# Revit family: Sunshade-Corner-Kawneer-Curtain_Wall-Inside_90
name_source: partatom
category: Specialty Equipment
revit_build: Autodesk Revit 2015 (Build: 20140905_0730(x64)
units: mm (PartAtom-declared; Revit-internal decimal feet)

## types (1)
- 30"-Circular-Square
    Angle 1 = 135.00°
    Blade 1 Location = 0' - 0"
    Blade 2 Location = 0' - 0"
    Blade 3 Location = 0' - 0"
    Blade 4 Location = 0' - 0"
    Blade 5 Location = 0' - 0"
    Blade 6 Location = 0' - 0"
    Blade Distance = 0' - 5"
    Blade Type = Blade-Kawneer-Angle_Cut-Circular : Versoleil
    Bottom Fascia Offset = 2' - 5 1/4"
    CTRL Angle = 135.00°
    CTRL Fascia Location = 0' - 0"
    CTRL Length of Blade = 3' - 5 9/16"
    CTRL Outrigger Angle = 0.00°
    Default Elevation = 4' - 0"
    Description = Rounded Outrigger, Bullnose Fascias
    Distance Blade 1 and 2 = 0' - 0"
    Distance Blade 2 and 3 = 0' - 0"
    Distance Blade 3 and 4 = 0' - 0"
    Distance Blade 4 and 5 = 0' - 0"
    Distance Blade 5 and 6 = 0' - 0"
    Fascia Type = Fascia-Kawneer-Inside_Angle_Cut-Rectangular : Versoleil
    Finish = Aluminum - Kawneer - Clear
    Has 5th Blade = Yes
    Has 6th Blade = No
    Height of Blade 1 = 0' - 5"
    Height of Bottom Fascia = 2' - 6"
    Length = 2' - 6"
    Manufacturer = Kawneer
    Model = Sunshade Inside 90 Degree Corner
    Outrigger Type = Outrigger-Kawneer-Angle-Square : 5"
    Product Documentation Link = http://www.kawneer.com
    Product Page URL = http://www.kawneer.com
    Product data url = https://bimobject.com
    Right Fascia Offset = 2' - 5 7/16"
    Set 1 Inset = 0' - 5 1/4"
    Set 2 Inset = 0' - 5 1/4"
    URL = http://www.kawneer.com

## geometry (parser evidence)
native form markers: Blend x6, Sweep x37
no freeform markers — native parametric forms only
